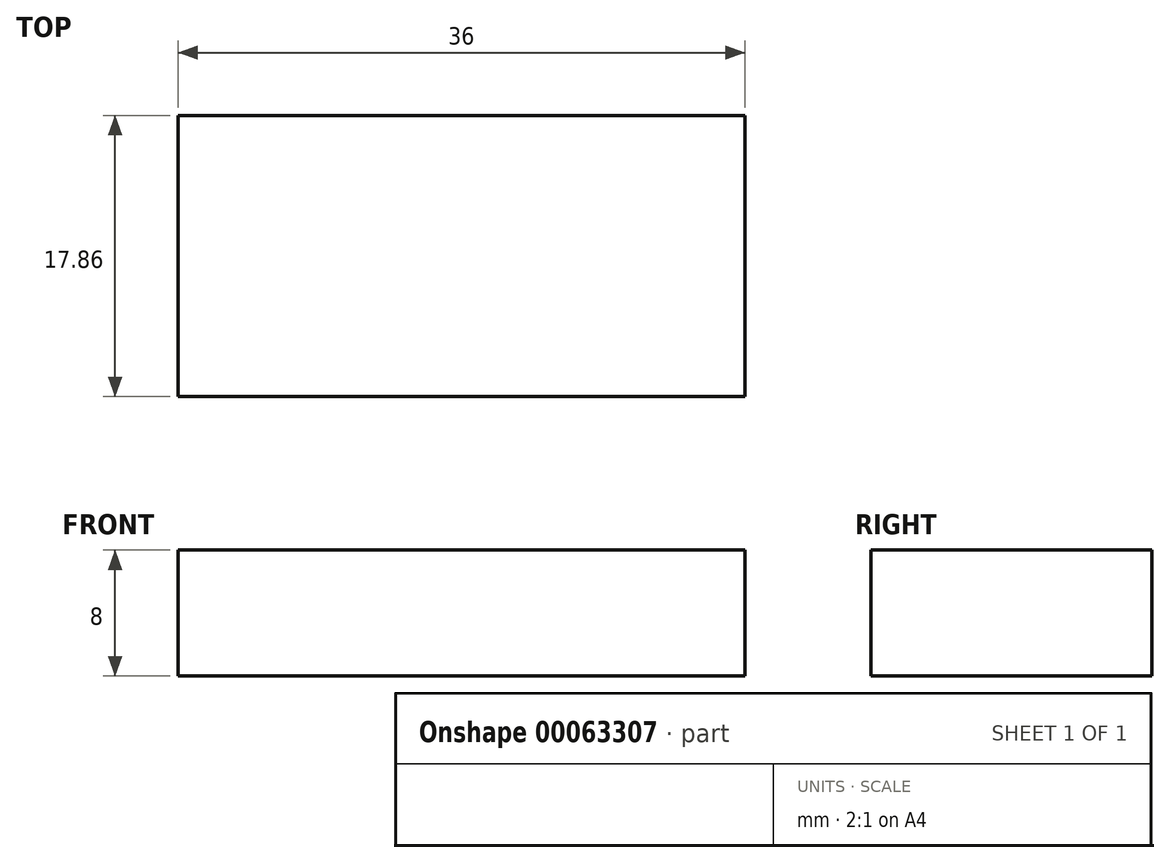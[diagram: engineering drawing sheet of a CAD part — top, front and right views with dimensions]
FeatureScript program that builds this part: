
annotation { "Feature Type Name" : "Feature", "Feature Type Description" : "" }
export const myFeature = defineFeature(function(context is Context, id is Id, definition is map)
    precondition{}
    {
        {
            var Q0;
            Q0=qCreatedBy(makeId("Top.planeOp"),FACE);
            var sketch = newSketch(context, id + "F0", { "sketchPlane" : qUnion([Q0])});
            skLineSegment(sketch, "E0.rect.bottom", {"start": v(18, -8.93) * mm, "end": v(-18, -8.93) * mm});
            skLineSegment(sketch, "E0.rect.top", {"start": v(18, 8.93) * mm, "end": v(-18, 8.93) * mm});
            skLineSegment(sketch, "E0.rect.left", {"start": v(18, -8.93) * mm, "end": v(18, 8.93) * mm});
            skLineSegment(sketch, "E0.rect.right", {"start": v(-18, -8.93) * mm, "end": v(-18, 8.93) * mm});
            skPoint(sketch, "E0.rect.middle", {"position": v(0, 0) * mm});
            skSolve(sketch);
        }
        {
            var Q0;
            Q0=makeQuery(id+"F0.imprint","IMPRINT",FACE,{"disambiguationData":[TD([[makeQuery(id+"F0.imprint","IMPRINT",EDGE,{"derivedFrom":sQuery(id+"F0.wireOp",EDGE,"E0.rect.bottom")}),-1.0]])]});
            extrude(context, id + "F1", {"entities" : qUnion([Q0]), "depth" : 8 * mm});
        }
    });
